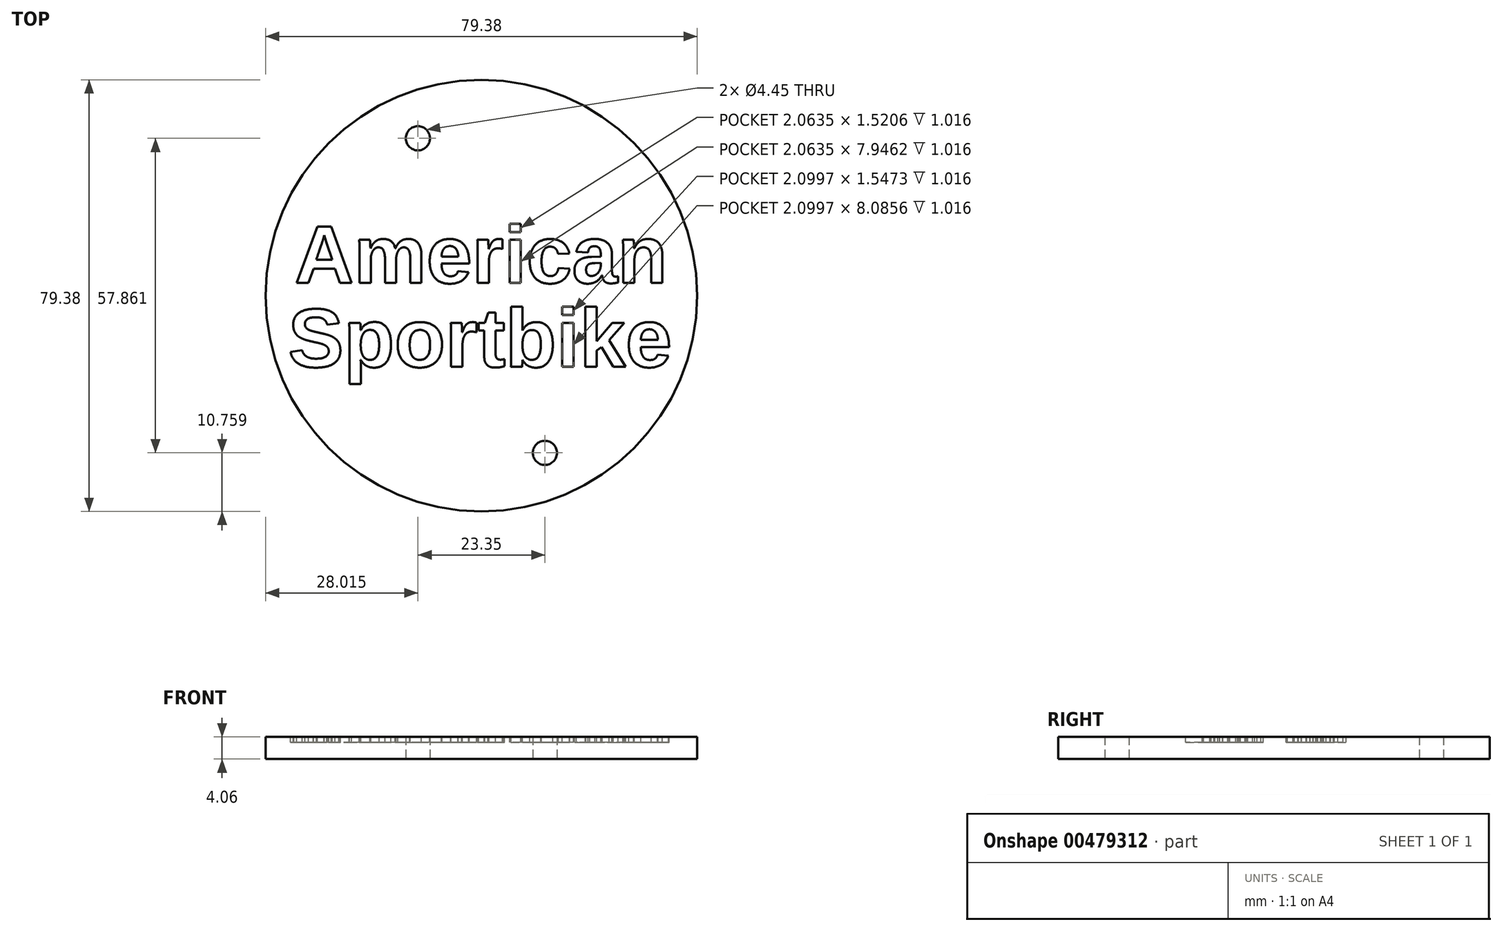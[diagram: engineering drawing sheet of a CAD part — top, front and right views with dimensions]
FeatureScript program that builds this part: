
annotation { "Feature Type Name" : "Feature", "Feature Type Description" : "" }
export const myFeature = defineFeature(function(context is Context, id is Id, definition is map)
    precondition{}
    {
        {
            var Q0;
            Q0=qCreatedBy(makeId("Top.planeOp"),FACE);
            var sketch = newSketch(context, id + "F0", { "sketchPlane" : qUnion([Q0])});
            skCircle(sketch, "E0", {"center": v(0, 0) * mm, "radius": 39.69 * mm});
            skCircle(sketch, "E1", {"center": v(-11.67, 28.93) * mm, "radius": 2.22 * mm});
            skCircle(sketch, "E2", {"center": v(11.67, -28.93) * mm, "radius": 2.22 * mm});
            skPoint(sketch, "E3", {"position": v(0, 39.69) * mm});
            skSolve(sketch);
        }
        {
            var Q0;
            Q0=makeQuery(id+"F0.imprint","IMPRINT",FACE,{"disambiguationData":[TD([[makeQuery(id+"F0.imprint","IMPRINT",EDGE,{"derivedFrom":sQuery(id+"F0.wireOp",EDGE,"E0")}),1.0]])]});
            extrude(context, id + "F1", {"entities" : qUnion([Q0]), "depth" : 4.06 * mm});
        }
        {
            var Q0;
            Q0=makeQuery(id+"F1.opExtrude","CAP_FACE",FACE,{"disambiguationData":[OSD([sQuery(id+"F0.wireOp",EDGE,"E0"),sQuery(id+"F0.wireOp",EDGE,"E1"),sQuery(id+"F0.wireOp",EDGE,"E2")])],"isStart":false});
            var sketch = newSketch(context, id + "F2", { "sketchPlane" : qUnion([Q0])});
            skText(sketch, "E4", { "text": "American", "fontName": "Arimo-Bold.ttf"});
            skText(sketch, "E5", { "text": "Sportbike", "fontName": "Arimo-Bold.ttf"});
            const initialGuessF2  = {"E4": [-0.03433, 0.00232, 1, 0, 0.01083], "E5": [-0.03555, -0.01311, 1, 0, 0.01102]};
            skSetInitialGuess(sketch, initialGuessF2);
            skSolve(sketch);
        }
        {
            var Q0;
            Q0=qSketchRegion(id+"F2",true);
            extrude(context, id + "F3", {"entities" : qUnion([Q0]), "operationType" : NewBodyOperationType.REMOVE, "oppositeDirection" : true, "depth" : 1.02 * mm});
        }
    });
